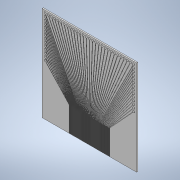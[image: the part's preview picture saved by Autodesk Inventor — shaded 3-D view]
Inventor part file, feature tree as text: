
AUTODESK INVENTOR PART (.ipt)
format: ipt  version: 2021 (Build 250183000, 183)  size: 1,195,008 bytes
history: native  units: in
note: dims shown in document units (in); Inventor stores cm internally (conversion verified against a paired STEP export)
features: extrude x5, sketch x4, projected_geometry x4, pattern_linear x2, mirror x1
ambient origin geometry x8: Origin, YZ Plane, XZ Plane, XY Plane, X Axis, Y Axis, Z Axis, Center Point
bodies: Solid1 (feature_tree)
feature tree (16):
  extrude  "Extrusion1"  Depth=2.9921in
  extrude  "Extrusion2"  Depth=0.0118in
  pattern_linear  "Rectangular Pattern1"  Count1=2  [1 undecoded]
  extrude  "Extrusion3"  Depth=0.0236in
  pattern_linear  "Rectangular Pattern2"  Count1=4  [1 undecoded]
  extrude  "Extrusion4"  Depth=0.0014in
  extrude  "Extrusion5"  Depth=0.0014in TaperAngle=0.0deg
  mirror  "Mirror1"
  sketch  "Sketch1"  dims[d0=2.9921in d1=2.9921in]
  sketch  "Sketch2"  dims[d2=0.0394in d3=0.0in d4=0.0118in d5=0.7874in]
  projected_geometry  "Projected Loop1"
  projected_geometry  "Projected Loop2"
  sketch  "Sketch4"  dims[d6=0.0014in d7=0.0in d8=21.6535in d10=0.0236in d11=1.5748in]
  projected_geometry  "Projected Loop3"
  sketch  "Sketch5"  dims[d12=0.1969in d13=0.0689in d16=0.0014in d17=0.0in d18=0.0787in d19=11.4173in d21=0.1in d22=5.5118in d24=0.1in d25=0.0118in d26=0.0118in d27=0.0118in d28=0.0118in d29=0.0118in d30=0.0118in d31=0.0118in d32=0.0118in d33=0.0118in d34=0.0118in d35=0.0118in d36=0.0118in d37=0.0118in d38=0.0118in d39=0.0118in d40=0.0118in d41=0.0118in d42=0.0118in d43=0.0118in d44=0.0118in d45=0.0118in d46=0.0118in d47=0.0118in d48=0.0118in d49=0.0118in d50=0.0118in d51=0.0118in d52=0.0118in d53=0.0014in d54=0.0in d55=0.0295in d56=0.0in d57=0.0in]
  projected_geometry  "Projected Loop4"
note: 2 required parameter values undecoded (feature->parameter linkage not recoverable at this tier; creation-order binding heuristic only, values carry confidence <= 0.55)
